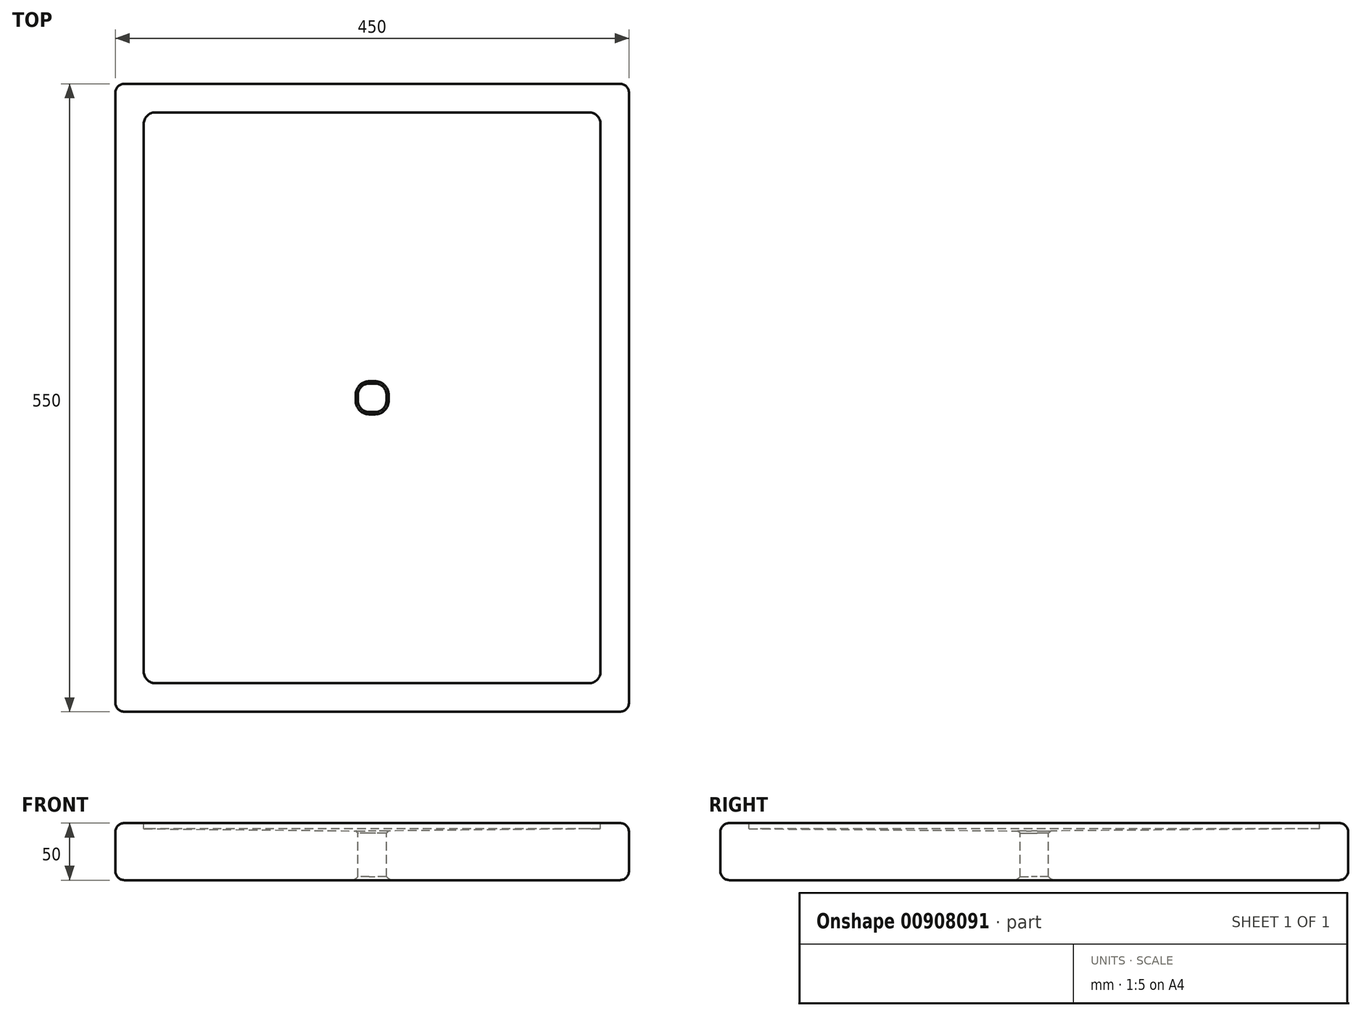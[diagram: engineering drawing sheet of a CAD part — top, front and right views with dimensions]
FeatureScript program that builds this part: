
annotation { "Feature Type Name" : "Feature", "Feature Type Description" : "" }
export const myFeature = defineFeature(function(context is Context, id is Id, definition is map)
    precondition{}
    {
        {
            var Q0;
            Q0=qCreatedBy(makeId("Top.planeOp"),FACE);
            var sketch = newSketch(context, id + "F0", { "sketchPlane" : qUnion([Q0])});
            skLineSegment(sketch, "E0.bottom", {"start": v(225, 275) * mm, "end": v(-225, 275) * mm});
            skLineSegment(sketch, "E0.top", {"start": v(225, -275) * mm, "end": v(-225, -275) * mm});
            skLineSegment(sketch, "E0.left", {"start": v(225, 275) * mm, "end": v(225, -275) * mm});
            skLineSegment(sketch, "E0.right", {"start": v(-225, 275) * mm, "end": v(-225, -275) * mm});
            skPoint(sketch, "E0.middle", {"position": v(0, 0) * mm});
            skSolve(sketch);
        }
        {
            var Q0;
            Q0=makeQuery(id+"F0.imprint","IMPRINT",FACE,{"disambiguationData":[TD([[makeQuery(id+"F0.imprint","IMPRINT",EDGE,{"derivedFrom":sQuery(id+"F0.wireOp",EDGE,"E0.bottom")}),1.0]])]});
            extrude(context, id + "F1", {"entities" : qUnion([Q0]), "oppositeDirection" : true, "depth" : 50 * mm, "offsetDistance" : 25 * mm});
        }
        {
            var Q0;
            Q0=makeQuery(id+"F1.opExtrude","CAP_FACE",FACE,{"disambiguationData":[OSD([sQuery(id+"F0.wireOp",EDGE,"E0.bottom"),sQuery(id+"F0.wireOp",EDGE,"E0.top"),sQuery(id+"F0.wireOp",EDGE,"E0.left"),sQuery(id+"F0.wireOp",EDGE,"E0.right")])],"isStart":true});
            var sketch = newSketch(context, id + "F2", { "sketchPlane" : qUnion([Q0])});
            skLineSegment(sketch, "E1.bottom", {"start": v(200, 250) * mm, "end": v(-200, 250) * mm});
            skLineSegment(sketch, "E1.top", {"start": v(200, -250) * mm, "end": v(-200, -250) * mm});
            skLineSegment(sketch, "E1.left", {"start": v(200, 250) * mm, "end": v(200, -250) * mm});
            skLineSegment(sketch, "E1.right", {"start": v(-200, 250) * mm, "end": v(-200, -250) * mm});
            skPoint(sketch, "E1.middle", {"position": v(0, 0) * mm});
            skSolve(sketch);
        }
        {
            var Q0;
            Q0=makeQuery(id+"F2.imprint","IMPRINT",FACE,{"disambiguationData":[TD([[makeQuery(id+"F2.imprint","IMPRINT",EDGE,{"derivedFrom":sQuery(id+"F2.wireOp",EDGE,"E1.bottom")}),-1.0]])]});
            cPlane(context, id + "F3", {"entities" : qUnion([Q0]), "cplaneType" : CPlaneType.OFFSET, "offset" : 7 * mm, "oppositeDirection" : true, "width" : 150 * mm, "height" : 150 * mm});
        }
        {
            var Q0;
            Q0=qCreatedBy(id+"F3.planeOp",FACE);
            var sketch = newSketch(context, id + "F4", { "sketchPlane" : qUnion([Q0])});
            skLineSegment(sketch, "E2.bottom", {"start": v(110, 110) * mm, "end": v(-110, 110) * mm});
            skLineSegment(sketch, "E2.top", {"start": v(110, -110) * mm, "end": v(-110, -110) * mm});
            skLineSegment(sketch, "E2.left", {"start": v(110, 110) * mm, "end": v(110, -110) * mm});
            skLineSegment(sketch, "E2.right", {"start": v(-110, 110) * mm, "end": v(-110, -110) * mm});
            skPoint(sketch, "E2.middle", {"position": v(0, 0) * mm});
            skSolve(sketch);
        }
        {
            var Q0;
            Q0 = qSketchRegion(id + "F2", true);
            extrude(context, id + "F5", {"entities" : qUnion([Q0]), "operationType" : NewBodyOperationType.REMOVE, "oppositeDirection" : true, "depth" : 5 * mm, "offsetDistance" : 25 * mm});
        }
        {
            var Q1;
            Q1=makeQuery(id+"F5.boolean.opBoolean","COPY",FACE,{"derivedFrom":makeQuery(id+"F5.opExtrude","CAP_FACE",FACE,{"disambiguationData":[OSD([sQuery(id+"F2.wireOp",EDGE,"E1.bottom"),sQuery(id+"F2.wireOp",EDGE,"E1.top"),sQuery(id+"F2.wireOp",EDGE,"E1.left"),sQuery(id+"F2.wireOp",EDGE,"E1.right")])],"isStart":false})});
            var Q2;
            Q2=sQuery(id+"F4.wireOp",VERTEX,"E2.middle");
            loft(context, id + "F6", {"operationType" : NewBodyOperationType.REMOVE, "sheetProfilesArray" : [{ "sheetProfileEntities" : qUnion([Q1]) }, { "sheetProfileEntities" : qUnion([Q2]) }]});
        }
        {
            var Q0;
            Q0=makeQuery(id+"F6.boolean.opBoolean","COPY",EDGE,{"derivedFrom":makeQuery(id+"F6.opLoft","SWEPT_EDGE",EDGE,{"disambiguationData":[OSD([sQuery(id+"F2.wireOp",EDGE,"E1.bottom"),sQuery(id+"F2.wireOp",EDGE,"E1.right"),sQuery(id+"F4.wireOp",VERTEX,"E2.middle")])]})});
            var Q1;
            Q1=makeQuery(id+"F6.boolean.opBoolean","COPY",EDGE,{"derivedFrom":makeQuery(id+"F6.opLoft","SWEPT_EDGE",EDGE,{"disambiguationData":[OSD([sQuery(id+"F2.wireOp",EDGE,"E1.bottom"),sQuery(id+"F2.wireOp",EDGE,"E1.left"),sQuery(id+"F4.wireOp",VERTEX,"E2.middle")])]})});
            var Q2;
            Q2=makeQuery(id+"F6.boolean.opBoolean","COPY",EDGE,{"derivedFrom":makeQuery(id+"F6.opLoft","SWEPT_EDGE",EDGE,{"disambiguationData":[OSD([sQuery(id+"F2.wireOp",EDGE,"E1.top"),sQuery(id+"F2.wireOp",EDGE,"E1.left"),sQuery(id+"F4.wireOp",VERTEX,"E2.middle")])]})});
            var Q3;
            Q3=makeQuery(id+"F6.boolean.opBoolean","COPY",EDGE,{"derivedFrom":makeQuery(id+"F6.opLoft","SWEPT_EDGE",EDGE,{"disambiguationData":[OSD([sQuery(id+"F2.wireOp",EDGE,"E1.top"),sQuery(id+"F2.wireOp",EDGE,"E1.right"),sQuery(id+"F4.wireOp",VERTEX,"E2.middle")])]})});
            fillet(context, id + "F7", {"entities" : qUnion([Q0, Q1, Q2, Q3]), "radius" : 1000 * mm, "tangentPropagation" : true, "allowEdgeOverflow" : false});
        }
        {
            var Q0;
            Q0=qCreatedBy(id+"F3.planeOp",FACE);
            var sketch = newSketch(context, id + "F8", { "sketchPlane" : qUnion([Q0])});
            skLineSegment(sketch, "E3.bottom", {"start": v(2.5, -12.5) * mm, "end": v(-2.5, -12.5) * mm});
            skLineSegment(sketch, "E3.top", {"start": v(2.5, 12.5) * mm, "end": v(-2.5, 12.5) * mm});
            skLineSegment(sketch, "E3.left", {"start": v(12.5, -2.5) * mm, "end": v(12.5, 2.5) * mm});
            skLineSegment(sketch, "E3.right", {"start": v(-12.5, -2.5) * mm, "end": v(-12.5, 2.5) * mm});
            skPoint(sketch, "E3.middle", {"position": v(0, 0) * mm});
            skPoint(sketch, "E4.visualSharp", {"position": v(-12.5, 12.5) * mm});
            skArc(sketch, "E4.filletArc", {"start": v(-2.5, 12.5) * mm, "mid": v(-9.57, 9.57) * mm, "end": v(-12.5, 2.5) * mm});
            skPoint(sketch, "E5.visualSharp", {"position": v(-12.5, -12.5) * mm});
            skArc(sketch, "E5.filletArc", {"start": v(-12.5, -2.5) * mm, "mid": v(-9.57, -9.57) * mm, "end": v(-2.5, -12.5) * mm});
            skPoint(sketch, "E6.visualSharp", {"position": v(12.5, 12.5) * mm});
            skArc(sketch, "E6.filletArc", {"start": v(12.5, 2.5) * mm, "mid": v(9.57, 9.57) * mm, "end": v(2.5, 12.5) * mm});
            skPoint(sketch, "E7.visualSharp", {"position": v(12.5, -12.5) * mm});
            skArc(sketch, "E7.filletArc", {"start": v(2.5, -12.5) * mm, "mid": v(9.57, -9.57) * mm, "end": v(12.5, -2.5) * mm});
            skSolve(sketch);
        }
        {
            var Q0;
            Q0 = qSketchRegion(id + "F8", true);
            extrude(context, id + "F9", {"entities" : qUnion([Q0]), "operationType" : NewBodyOperationType.REMOVE, "oppositeDirection" : true, "depth" : 50 * mm, "offsetDistance" : 25 * mm, "hasSecondDirection" : true, "secondDirectionOppositeDirection" : false, "secondDirectionDepth" : 25 * mm});
        }
        {
            var Q0;
            Q0=makeQuery(id+"F9.boolean.opBoolean","INTERSECT",EDGE,{"derivedFrom":[makeQuery(id+"F6.boolean.opBoolean","COPY",FACE,{"derivedFrom":makeQuery(id+"F6.opLoft","SWEPT_FACE",FACE,{"disambiguationData":[OSD([sQuery(id+"F2.wireOp",EDGE,"E1.bottom"),sQuery(id+"F2.wireOp",EDGE,"E1.left"),sQuery(id+"F2.wireOp",EDGE,"E1.right")])]})}),makeQuery(id+"F9.opExtrude","SWEPT_FACE",FACE,{"disambiguationData":[OSD([sQuery(id+"F8.wireOp",EDGE,"E3.top")])]})]});
            chamfer(context, id + "F10", {"entities" : qUnion([Q0]), "width" : 2 * mm, "tangentPropagation" : true});
        }
        {
            var Q0;
            Q0=makeQuery(id+"F9.boolean.opBoolean","INTERSECT",EDGE,{"derivedFrom":[makeQuery(id+"F1.opExtrude","CAP_FACE",FACE,{"disambiguationData":[OSD([sQuery(id+"F0.wireOp",EDGE,"E0.bottom"),sQuery(id+"F0.wireOp",EDGE,"E0.top"),sQuery(id+"F0.wireOp",EDGE,"E0.left"),sQuery(id+"F0.wireOp",EDGE,"E0.right")])],"isStart":false}),makeQuery(id+"F9.opExtrude","SWEPT_FACE",FACE,{"disambiguationData":[OSD([sQuery(id+"F8.wireOp",EDGE,"E4.filletArc")])]})]});
            chamfer(context, id + "F11", {"entities" : qUnion([Q0]), "width" : 3 * mm, "tangentPropagation" : true});
        }
        {
            var Q0;
            Q0=makeQuery(id+"F1.opExtrude","CAP_EDGE",EDGE,{"disambiguationData":[OSD([sQuery(id+"F0.wireOp",EDGE,"E0.top")])],"isStart":false});
            var Q1;
            Q1=makeQuery(id+"F1.opExtrude","CAP_FACE",FACE,{"disambiguationData":[OSD([sQuery(id+"F0.wireOp",EDGE,"E0.bottom"),sQuery(id+"F0.wireOp",EDGE,"E0.top"),sQuery(id+"F0.wireOp",EDGE,"E0.left"),sQuery(id+"F0.wireOp",EDGE,"E0.right")])],"isStart":false});
            var Q2;
            Q2=makeQuery(id+"F1.opExtrude","SWEPT_EDGE",EDGE,{"disambiguationData":[OSD([sQuery(id+"F0.wireOp",EDGE,"E0.top"),sQuery(id+"F0.wireOp",EDGE,"E0.right")])]});
            var Q3;
            Q3=makeQuery(id+"F1.opExtrude","SWEPT_EDGE",EDGE,{"disambiguationData":[OSD([sQuery(id+"F0.wireOp",EDGE,"E0.top"),sQuery(id+"F0.wireOp",EDGE,"E0.left")])]});
            var Q4;
            Q4=makeQuery(id+"F1.opExtrude","SWEPT_EDGE",EDGE,{"disambiguationData":[OSD([sQuery(id+"F0.wireOp",EDGE,"E0.bottom"),sQuery(id+"F0.wireOp",EDGE,"E0.left")])]});
            var Q5;
            Q5=makeQuery(id+"F1.opExtrude","SWEPT_EDGE",EDGE,{"disambiguationData":[OSD([sQuery(id+"F0.wireOp",EDGE,"E0.bottom"),sQuery(id+"F0.wireOp",EDGE,"E0.right")])]});
            var Q6;
            Q6=makeQuery(id+"F1.opExtrude","CAP_EDGE",EDGE,{"disambiguationData":[OSD([sQuery(id+"F0.wireOp",EDGE,"E0.right")])],"isStart":true});
            var Q7;
            Q7=makeQuery(id+"F1.opExtrude","CAP_EDGE",EDGE,{"disambiguationData":[OSD([sQuery(id+"F0.wireOp",EDGE,"E0.bottom")])],"isStart":true});
            var Q8;
            Q8=makeQuery(id+"F1.opExtrude","CAP_EDGE",EDGE,{"disambiguationData":[OSD([sQuery(id+"F0.wireOp",EDGE,"E0.left")])],"isStart":true});
            var Q9;
            Q9=makeQuery(id+"F1.opExtrude","CAP_EDGE",EDGE,{"disambiguationData":[OSD([sQuery(id+"F0.wireOp",EDGE,"E0.top")])],"isStart":true});
            fillet(context, id + "F12", {"entities" : qUnion([Q0, Q1, Q2, Q3, Q4, Q5, Q6, Q7, Q8, Q9]), "radius" : 8 * mm, "tangentPropagation" : true, "allowEdgeOverflow" : false});
        }
        {
            var Q0;
            Q0=makeQuery(id+"F5.boolean.opBoolean","COPY",EDGE,{"derivedFrom":makeQuery(id+"F5.opExtrude","SWEPT_EDGE",EDGE,{"disambiguationData":[OSD([sQuery(id+"F2.wireOp",EDGE,"E1.bottom"),sQuery(id+"F2.wireOp",EDGE,"E1.right")])]})});
            var Q1;
            Q1=makeQuery(id+"F5.boolean.opBoolean","COPY",EDGE,{"derivedFrom":makeQuery(id+"F5.opExtrude","SWEPT_EDGE",EDGE,{"disambiguationData":[OSD([sQuery(id+"F2.wireOp",EDGE,"E1.bottom"),sQuery(id+"F2.wireOp",EDGE,"E1.left")])]})});
            var Q2;
            Q2=makeQuery(id+"F5.boolean.opBoolean","COPY",EDGE,{"derivedFrom":makeQuery(id+"F5.opExtrude","SWEPT_EDGE",EDGE,{"disambiguationData":[OSD([sQuery(id+"F2.wireOp",EDGE,"E1.top"),sQuery(id+"F2.wireOp",EDGE,"E1.right")])]})});
            var Q3;
            Q3=makeQuery(id+"F5.boolean.opBoolean","COPY",EDGE,{"derivedFrom":makeQuery(id+"F5.opExtrude","SWEPT_EDGE",EDGE,{"disambiguationData":[OSD([sQuery(id+"F2.wireOp",EDGE,"E1.top"),sQuery(id+"F2.wireOp",EDGE,"E1.left")])]})});
            fillet(context, id + "F13", {"entities" : qUnion([Q0, Q1, Q2, Q3]), "radius" : 10 * mm, "tangentPropagation" : true, "allowEdgeOverflow" : false});
        }
    });
